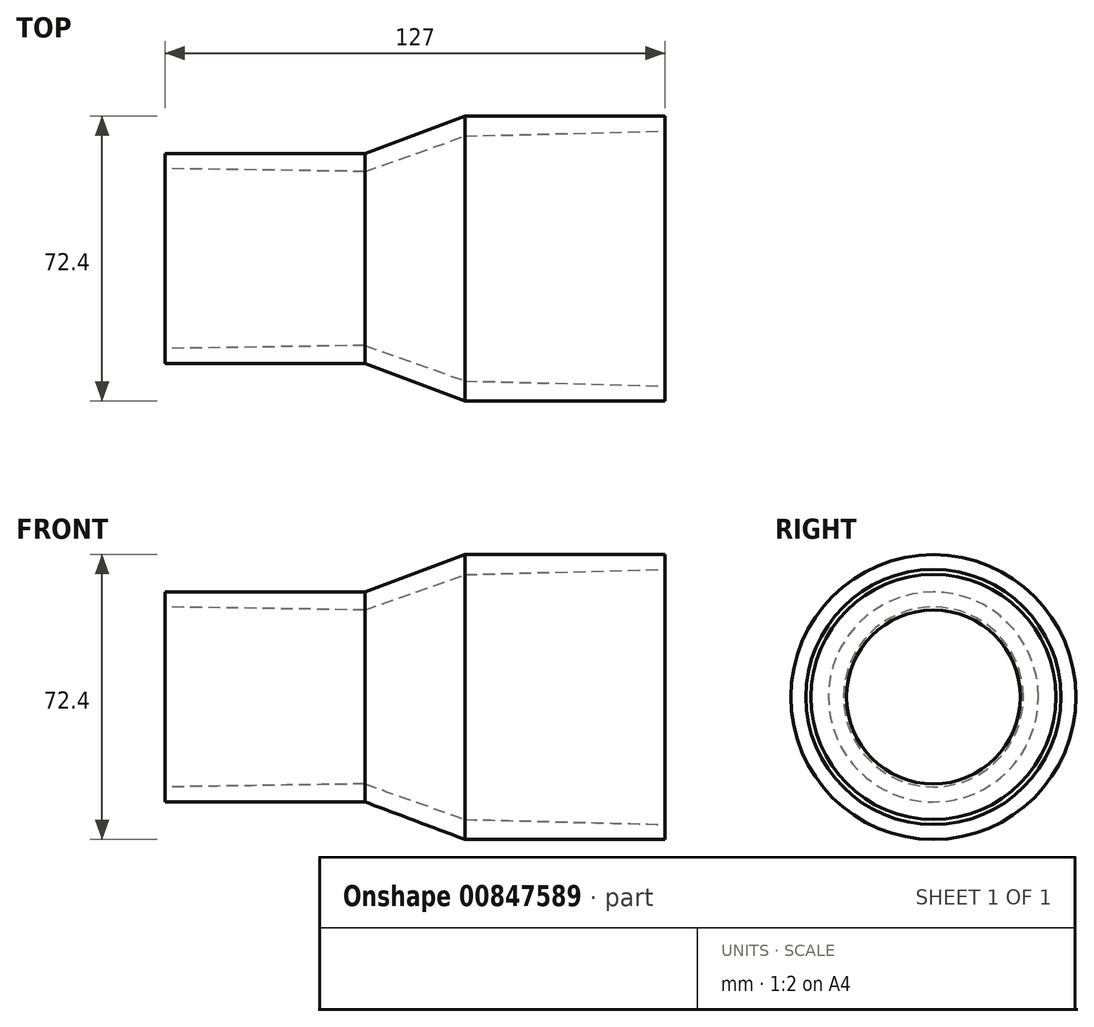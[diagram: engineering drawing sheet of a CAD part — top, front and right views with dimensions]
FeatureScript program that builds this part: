
annotation { "Feature Type Name" : "Feature", "Feature Type Description" : "" }
export const myFeature = defineFeature(function(context is Context, id is Id, definition is map)
    precondition{}
    {
        {
            var Q0;
            Q0=qCreatedBy(makeId("Front.planeOp"),FACE);
            var sketch = newSketch(context, id + "F0", { "sketchPlane" : qUnion([Q0])});
            skLineSegment(sketch, "E0", {"start": v(0, 0) * mm, "end": v(-79.5, 0) * mm, "construction": true});
            skLineSegment(sketch, "E1", {"start": v(0, 36.2) * mm, "end": v(50.8, 36.2) * mm});
            skLineSegment(sketch, "E2", {"start": v(50.8, 36.2) * mm, "end": v(50.8, 32.39) * mm});
            skLineSegment(sketch, "E3", {"start": v(50.8, 32.39) * mm, "end": v(0, 31.12) * mm});
            skLineSegment(sketch, "E4", {"start": v(0, 31.11) * mm, "end": v(-25.4, 22.1) * mm});
            skLineSegment(sketch, "E5", {"start": v(-25.4, 22.1) * mm, "end": v(-76.2, 22.86) * mm});
            skLineSegment(sketch, "E6", {"start": v(-76.2, 22.86) * mm, "end": v(-76.2, 26.67) * mm});
            skLineSegment(sketch, "E7", {"start": v(-76.2, 26.67) * mm, "end": v(-25.4, 26.67) * mm});
            skLineSegment(sketch, "E8", {"start": v(-25.4, 26.67) * mm, "end": v(0, 36.2) * mm});
            skPoint(sketch, "E9", {"position": v(25.4, 31.75) * mm});
            skPoint(sketch, "E10", {"position": v(-50.8, 22.48) * mm});
            skSolve(sketch);
        }
        {
            var Q0;
            Q0 = qSketchRegion(id + "F0", true);
            var Q1;
            Q1=sQuery(id+"F0.wireOp",EDGE,"E0");
            revolve(context, id + "F1", {"surfaceOperationType" : NewSurfaceOperationType.NEW, "entities" : qUnion([Q0]), "axis" : qUnion([Q1]), "revolveType" : RevolveType.FULL});
        }
    });
